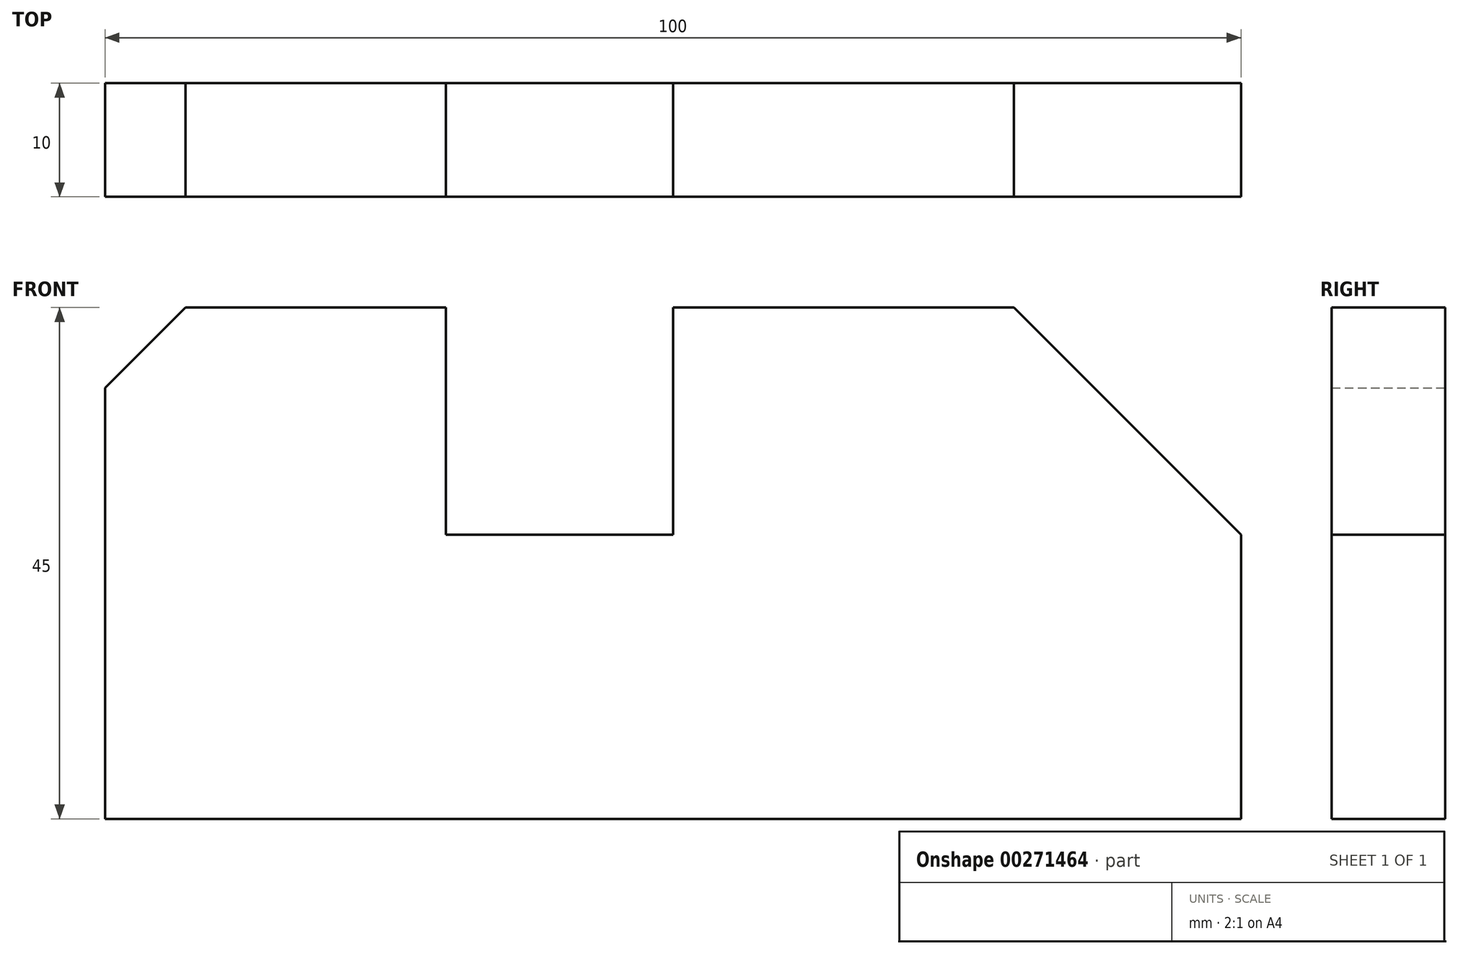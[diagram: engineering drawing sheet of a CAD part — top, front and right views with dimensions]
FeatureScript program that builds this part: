
annotation { "Feature Type Name" : "Feature", "Feature Type Description" : "" }
export const myFeature = defineFeature(function(context is Context, id is Id, definition is map)
    precondition{}
    {
        {
            var Q0;
            Q0=qCreatedBy(makeId("Front.planeOp"),FACE);
            var sketch = newSketch(context, id + "F0", { "sketchPlane" : qUnion([Q0])});
            skLineSegment(sketch, "E0", {"start": v(0, 0) * mm, "end": v(100, 0) * mm});
            skLineSegment(sketch, "E1", {"start": v(0, 0) * mm, "end": v(0, 37.93) * mm});
            skLineSegment(sketch, "E2", {"start": v(7.07, 45) * mm, "end": v(0, 37.93) * mm});
            skLineSegment(sketch, "E3", {"start": v(7.07, 45) * mm, "end": v(30, 45) * mm});
            skLineSegment(sketch, "E4", {"start": v(30, 45) * mm, "end": v(30, 25) * mm});
            skLineSegment(sketch, "E5", {"start": v(30, 25) * mm, "end": v(50, 25) * mm});
            skLineSegment(sketch, "E6", {"start": v(50, 25) * mm, "end": v(50, 45) * mm});
            skLineSegment(sketch, "E7", {"start": v(50, 45) * mm, "end": v(80, 45) * mm});
            skLineSegment(sketch, "E8", {"start": v(80, 45) * mm, "end": v(100, 25) * mm});
            skLineSegment(sketch, "E9", {"start": v(100, 25) * mm, "end": v(100, 0) * mm});
            skSolve(sketch);
        }
        {
            var Q0;
            Q0=makeQuery(id+"F0.imprint","IMPRINT",FACE,{"disambiguationData":[TD([[makeQuery(id+"F0.imprint","IMPRINT",EDGE,{"derivedFrom":sQuery(id+"F0.wireOp",EDGE,"E0")}),1.0]])]});
            extrude(context, id + "F1", {"entities" : qUnion([Q0]), "depth" : 10 * mm});
        }
    });
